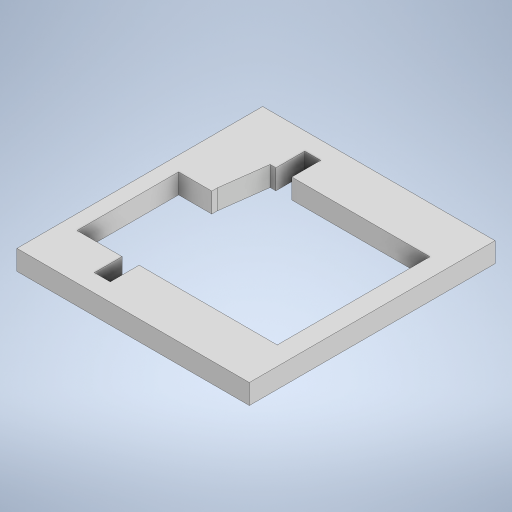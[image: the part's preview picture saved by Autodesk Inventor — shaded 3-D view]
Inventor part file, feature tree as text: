
AUTODESK INVENTOR PART (.ipt)
format: ipt  version: 2023.1 (Build 271208000, 208)  size: 259,072 bytes
history: native  units: mm
features: extrude x1, sketch x1
ambient origin geometry x8: Origin, YZ Plane, XZ Plane, XY Plane, X Axis, Y Axis, Z Axis, Center Point
bodies: Body1 (feature_tree)
feature tree (2):
  extrude  "Extrusion5"  Depth=4.35mm
  sketch  "Sketch1"  dims[d0=20.8mm d1=22.6mm d2=2.0mm d5=22.6mm d8=1.0mm d9=7.2mm d10=3.0mm d11=35.0mm d12=37.0mm d16=2.0mm d19=4.35mm d26=6.8mm d27=0.9mm d28=14.9mm d29=5.0mm d32=0.2mm d33=3.0mm d34=0.0mm d35=4.35mm]
